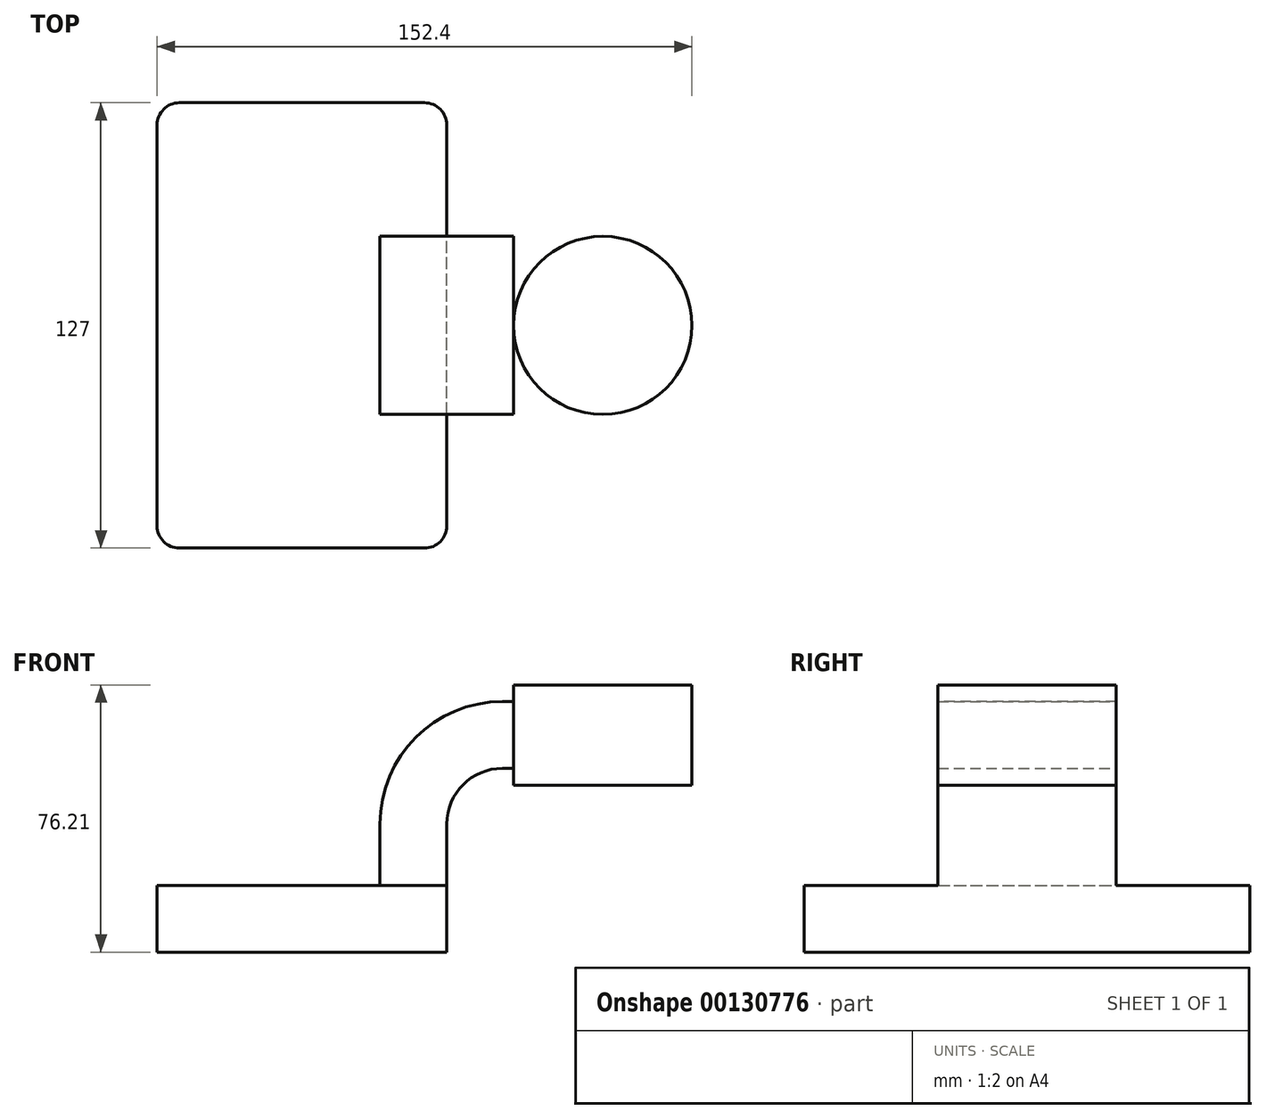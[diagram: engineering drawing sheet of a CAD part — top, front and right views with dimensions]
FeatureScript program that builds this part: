
annotation { "Feature Type Name" : "Feature", "Feature Type Description" : "" }
export const myFeature = defineFeature(function(context is Context, id is Id, definition is map)
    precondition{}
    {
        {
            var Q0;
            Q0=qCreatedBy(makeId("Front.planeOp"),FACE);
            var sketch = newSketch(context, id + "F0", { "sketchPlane" : qUnion([Q0])});
            skLineSegment(sketch, "E0.bottom", {"start": v(-41.28, 9.53) * mm, "end": v(41.28, 9.53) * mm});
            skLineSegment(sketch, "E0.top", {"start": v(-41.28, -9.53) * mm, "end": v(41.28, -9.53) * mm});
            skLineSegment(sketch, "E0.left", {"start": v(-41.28, 9.52) * mm, "end": v(-41.28, -9.53) * mm});
            skLineSegment(sketch, "E0.right", {"start": v(41.28, 9.53) * mm, "end": v(41.28, -9.52) * mm});
            skPoint(sketch, "E0.middle", {"position": v(0, 0) * mm});
            skLineSegment(sketch, "E1.bottom", {"start": v(111.12, 38.1) * mm, "end": v(60.32, 38.1) * mm});
            skLineSegment(sketch, "E1.top", {"start": v(111.12, 66.67) * mm, "end": v(60.32, 66.67) * mm});
            skLineSegment(sketch, "E1.left", {"start": v(111.13, 38.1) * mm, "end": v(111.13, 66.68) * mm});
            skLineSegment(sketch, "E1.right", {"start": v(60.33, 38.1) * mm, "end": v(60.33, 66.67) * mm});
            skPoint(sketch, "E1.middle", {"position": v(85.72, 52.39) * mm});
            skLineSegment(sketch, "E2", {"start": v(41.28, 9.53) * mm, "end": v(41.28, 27) * mm});
            skArc(sketch, "E3", {"start": v(41.28, 27) * mm, "mid": v(45.92, 38.23) * mm, "end": v(57.15, 42.88) * mm});
            skLineSegment(sketch, "E4", {"start": v(57.15, 42.88) * mm, "end": v(85.72, 42.88) * mm});
            skLineSegment(sketch, "E5.0", {"start": v(57.15, 61.93) * mm, "end": v(85.72, 61.93) * mm});
            skArc(sketch, "E5.1", {"start": v(22.23, 27) * mm, "mid": v(32.45, 51.7) * mm, "end": v(57.15, 61.93) * mm});
            skLineSegment(sketch, "E5.2", {"start": v(22.23, 9.52) * mm, "end": v(22.23, 27) * mm});
            skLineSegment(sketch, "E6", {"start": v(85.73, 38.1) * mm, "end": v(85.73, 66.68) * mm});
            skFitSpline(sketch, "E7", {"points": [v(-41.28, 9.52) * mm, v(57.15, 61.93) * mm, v(60.33, 61.93) * mm], "startDerivative": vector(0, 182.27) * mm, "endDerivative": vector(17.88, 0.25) * mm});
            skLineSegment(sketch, "E8", {"start": v(60.33, 61.93) * mm, "end": v(60.33, 42.88) * mm});
            skLineSegment(sketch, "E9", {"start": v(85.72, 61.93) * mm, "end": v(85.72, 42.88) * mm});
            skSolve(sketch);
        }
        {
            var Q0;
            Q0=makeQuery(id+"F0.imprint","IMPRINT",FACE,{"disambiguationData":[TD([[makeQuery(id+"F0.imprint","IMPRINT",EDGE,{"derivedFrom":sQuery(id+"F0.wireOp",EDGE,"E0.top")}),1.0]])]});
            extrude(context, id + "F1", {"entities" : qUnion([Q0]), "endBound" : BoundingType.SYMMETRIC, "depth" : 127 * mm});
        }
        {
            var Q0;
            {var subQ2=sQuery(id+"F0.wireOp",EDGE,"E8");Q0=makeQuery(id+"F0.imprint","IMPRINT",FACE,{"disambiguationData":[TD([[makeQuery(id+"F0.imprint","IMPRINT",EDGE,{"derivedFrom":subQ2}),1.0]])]});}
            var Q1;
            {var subQ5=sQuery(id+"F0.wireOp",EDGE,"E2");Q1=makeQuery(id+"F0.imprint","IMPRINT",FACE,{"disambiguationData":[TD([[makeQuery(id+"F0.imprint","IMPRINT",EDGE,{"derivedFrom":subQ5}),1.0]])]});}
            extrude(context, id + "F2", {"entities" : qUnion([Q0, Q1]), "operationType" : NewBodyOperationType.ADD, "endBound" : BoundingType.SYMMETRIC, "depth" : 50.8 * mm});
        }
        {
            var Q0;
            {var subQ5=sQuery(id+"F0.wireOp",EDGE,"E5.1");Q0=makeQuery(id+"F0.imprint","IMPRINT",FACE,{"disambiguationData":[TD([[makeQuery(id+"F0.imprint","IMPRINT",EDGE,{"derivedFrom":subQ5}),1.0]])]});}
            extrude(context, id + "F3", {"entities" : qUnion([Q0]), "operationType" : NewBodyOperationType.ADD, "endBound" : BoundingType.SYMMETRIC, "depth" : 15.88 * mm});
        }
        {
            var Q0;
            {var subQ0=sQuery(id+"F0.wireOp",EDGE,"E1.left");Q0=makeQuery(id+"F0.imprint","IMPRINT",FACE,{"disambiguationData":[TD([[makeQuery(id+"F0.imprint","IMPRINT",EDGE,{"derivedFrom":subQ0}),1.0]])]});}
            var Q1;
            Q1=sQuery(id+"F0.wireOp",EDGE,"E6");
            revolve(context, id + "F4", {"operationType" : NewBodyOperationType.ADD, "entities" : qUnion([Q0]), "axis" : qUnion([Q1]), "revolveType" : RevolveType.FULL});
        }
        {
            var Q0;
            Q0=makeQuery(id+"F1.opExtrude","CAP_EDGE",EDGE,{"disambiguationData":[OSD([sQuery(id+"F0.wireOp",EDGE,"E0.right")])],"isStart":false});
            var Q1;
            Q1=makeQuery(id+"F1.opExtrude","CAP_EDGE",EDGE,{"disambiguationData":[OSD([sQuery(id+"F0.wireOp",EDGE,"E0.left")])],"isStart":false});
            var Q2;
            Q2=makeQuery(id+"F1.opExtrude","CAP_EDGE",EDGE,{"disambiguationData":[OSD([sQuery(id+"F0.wireOp",EDGE,"E0.right")])],"isStart":true});
            var Q3;
            Q3=makeQuery(id+"F1.opExtrude","CAP_EDGE",EDGE,{"disambiguationData":[OSD([sQuery(id+"F0.wireOp",EDGE,"E0.left")])],"isStart":true});
            fillet(context, id + "F5", {"entities" : qUnion([Q0, Q1, Q2, Q3]), "radius" : 6.35 * mm, "tangentPropagation" : true, "allowEdgeOverflow" : false});
        }
    });
